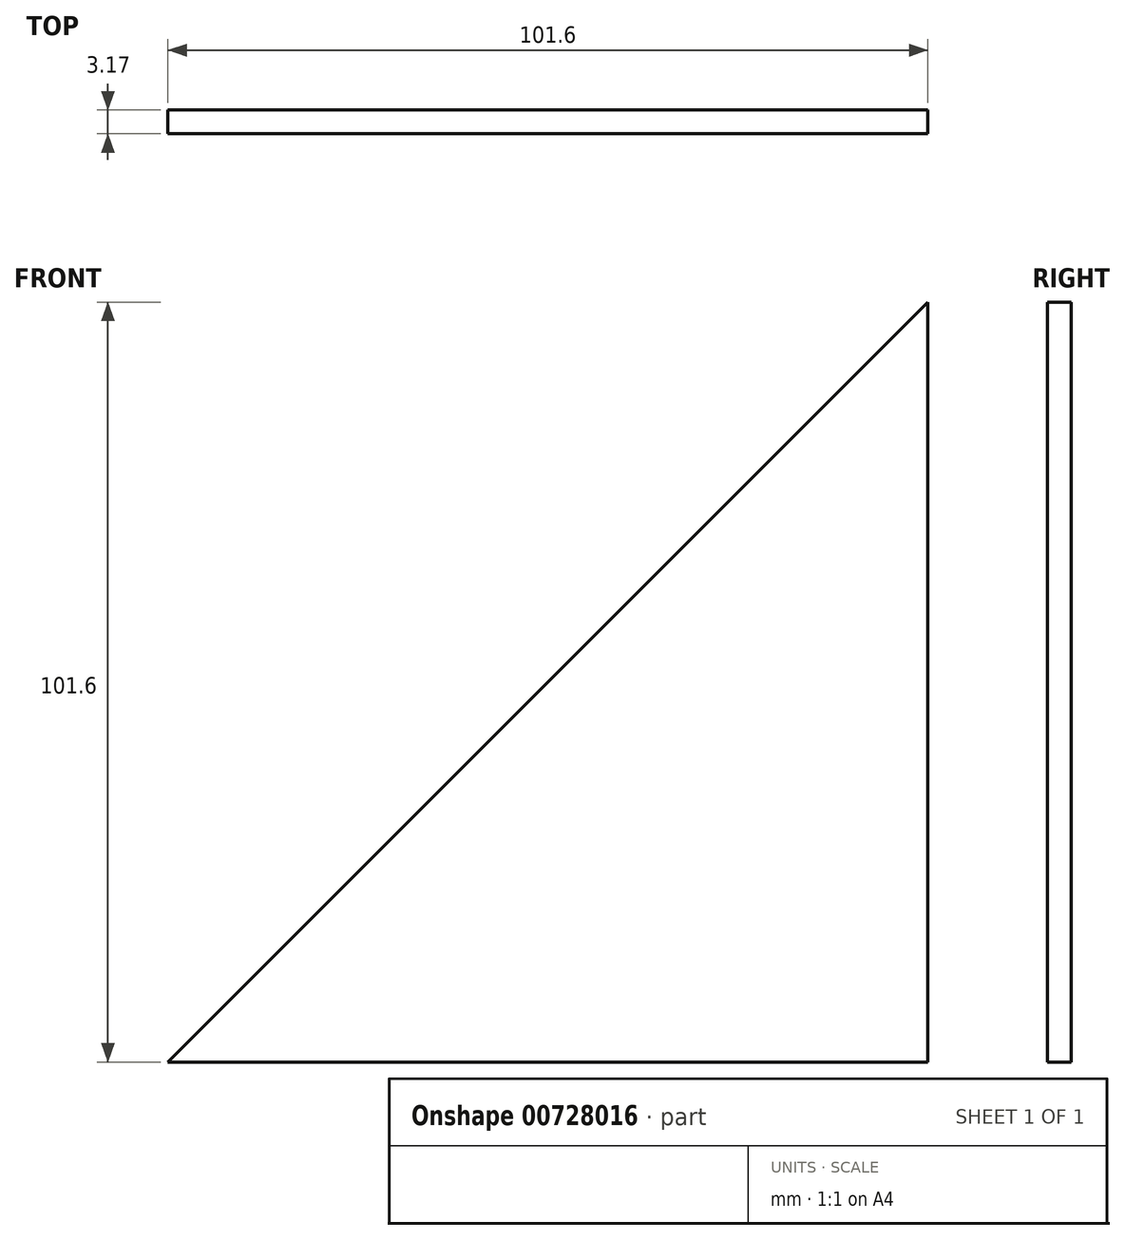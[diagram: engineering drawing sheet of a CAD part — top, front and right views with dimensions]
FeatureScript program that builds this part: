
annotation { "Feature Type Name" : "Feature", "Feature Type Description" : "" }
export const myFeature = defineFeature(function(context is Context, id is Id, definition is map)
    precondition{}
    {
        {
            var Q0;
            Q0=qCreatedBy(makeId("Front.planeOp"),FACE);
            var sketch = newSketch(context, id + "F0", { "sketchPlane" : qUnion([Q0])});
            skLineSegment(sketch, "E0", {"start": v(0, 0) * mm, "end": v(0, 101.6) * mm});
            skLineSegment(sketch, "E1", {"start": v(0, 101.6) * mm, "end": v(-101.6, 0) * mm});
            skLineSegment(sketch, "E2", {"start": v(-101.6, 0) * mm, "end": v(0, 0) * mm});
            skSolve(sketch);
        }
        {
            var Q0;
            Q0=makeQuery(id+"F0.imprint","IMPRINT",FACE,{"disambiguationData":[TD([[makeQuery(id+"F0.imprint","IMPRINT",EDGE,{"derivedFrom":sQuery(id+"F0.wireOp",EDGE,"E0")}),1.0]])]});
            extrude(context, id + "F1", {"entities" : qUnion([Q0]), "depth" : 3.17 * mm, "offsetDistance" : 25.4 * mm});
        }
    });
